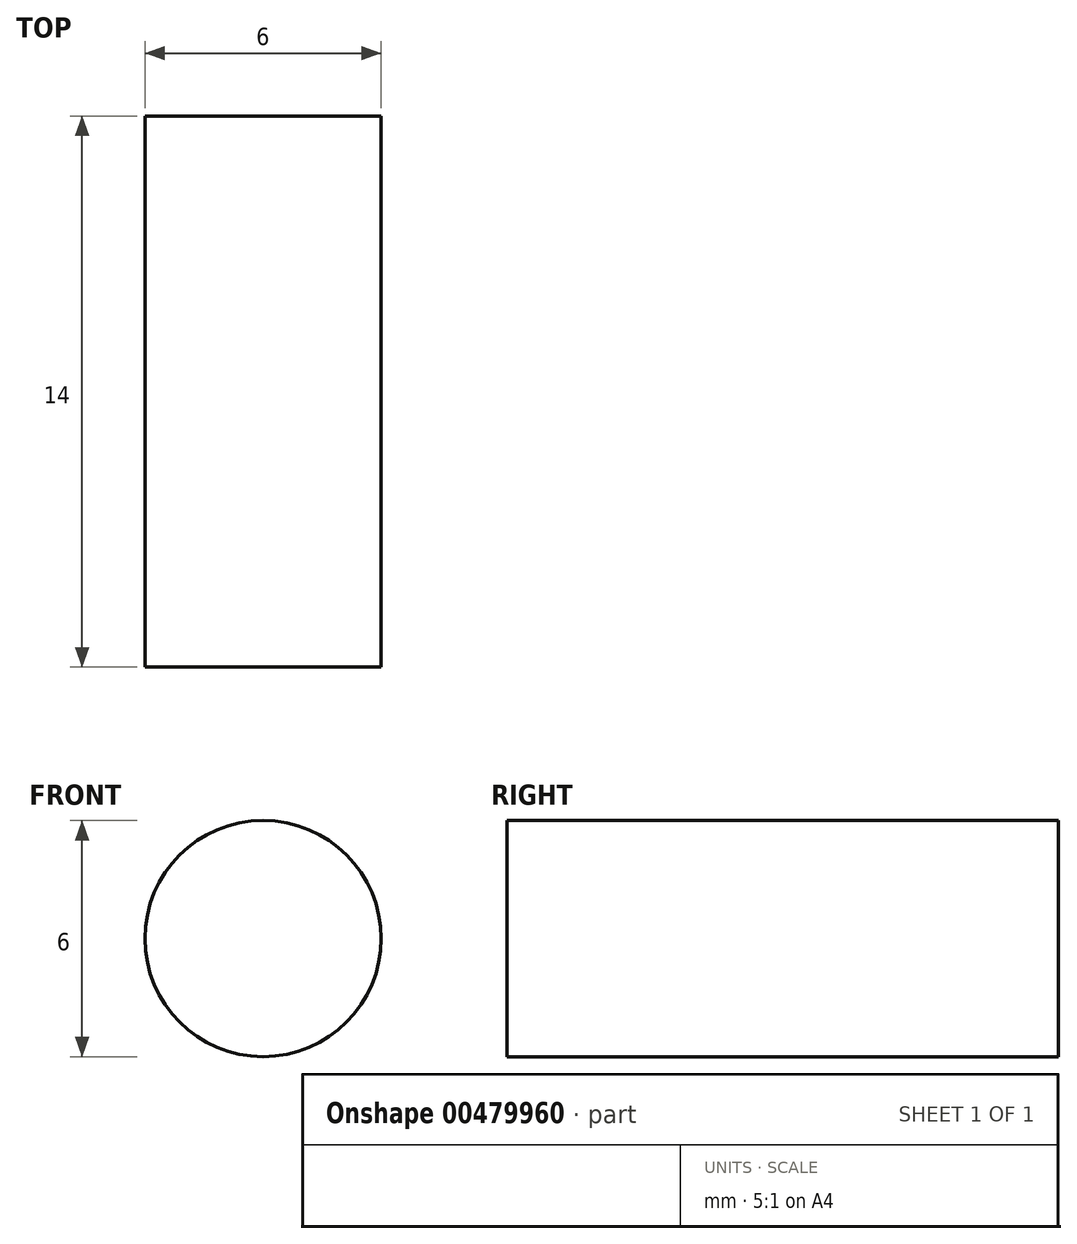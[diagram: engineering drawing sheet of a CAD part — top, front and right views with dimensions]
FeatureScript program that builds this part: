
annotation { "Feature Type Name" : "Feature", "Feature Type Description" : "" }
export const myFeature = defineFeature(function(context is Context, id is Id, definition is map)
    precondition{}
    {
        {
            var Q0;
            Q0=qCreatedBy(makeId("Front.planeOp"),FACE);
            var sketch = newSketch(context, id + "F0", { "sketchPlane" : qUnion([Q0])});
            skCircle(sketch, "E0", {"center": v(0, 0) * mm, "radius": 3 * mm});
            skSolve(sketch);
        }
        {
            var Q0;
            Q0=makeQuery(id+"F0.imprint","IMPRINT",FACE,{"disambiguationData":[TD([[makeQuery(id+"F0.imprint","IMPRINT",EDGE,{"derivedFrom":sQuery(id+"F0.wireOp",EDGE,"E0")}),1.0]])]});
            extrude(context, id + "F1", {"entities" : qUnion([Q0]), "depth" : 14 * mm});
        }
    });
